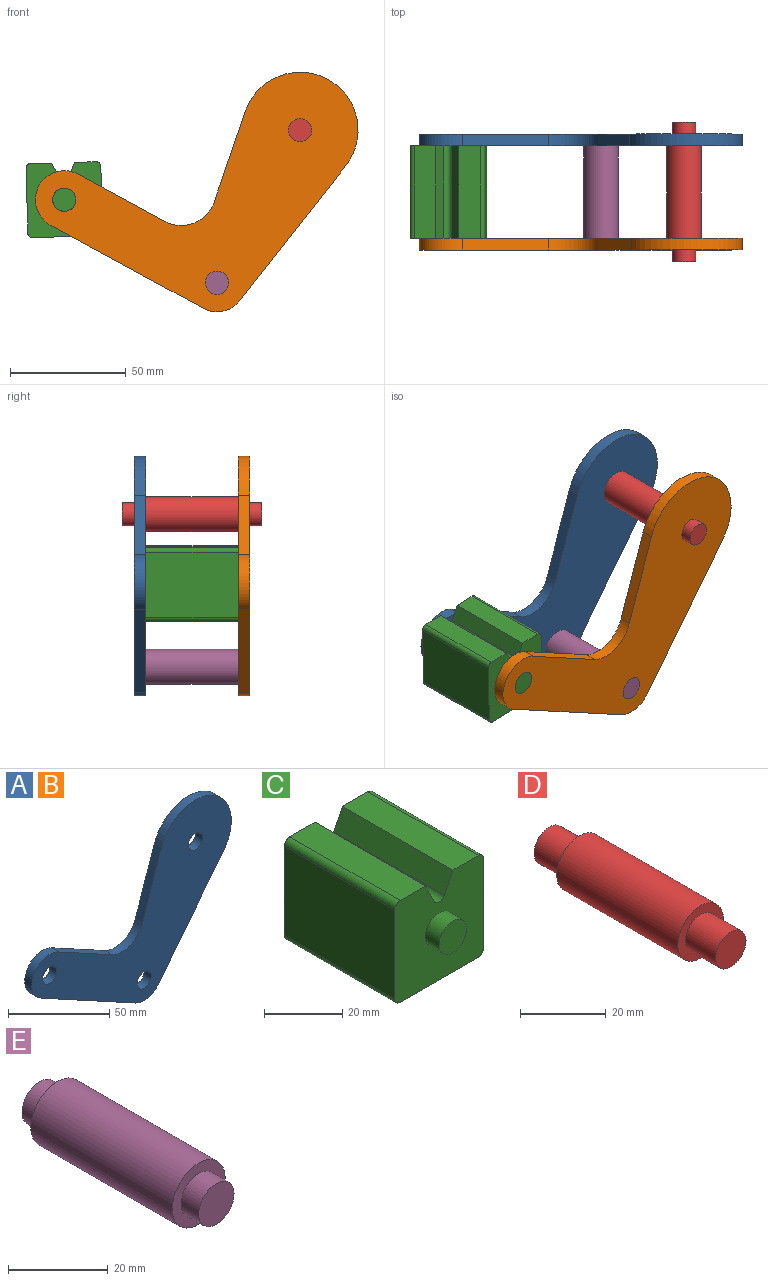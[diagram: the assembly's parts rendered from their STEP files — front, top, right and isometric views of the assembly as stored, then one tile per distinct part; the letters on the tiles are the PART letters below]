
ASSEMBLY  parts=5 mates=2
PART A: 13 faces, bbox 139.2x5x103.4 mm
  f0: cylinder r=25mm len=48.64mm, axis (0,-1,0), area 434.6mm2, adj f1,f9,f11,f12
  f1: plane 39.16x13.47mm, normal (-0.95,0,0.33), area 207.1mm2, adj f0,f2,f11,f12
  f2: cylinder r=15mm len=21.36mm, axis (0,-1,0), area 130.4mm2, adj f1,f3,f11,f12
  f3: plane 37.29x20.31mm, normal (0.48,0,0.88), area 212.3mm2, adj f2,f4,f11,f12
  f4: cylinder r=12.5mm len=23.48mm, axis (0,-1,0), area 196.3mm2, adj f3,f5,f11,f12
  f5: plane 65.87x35.87mm, normal (-0.48,0,-0.88), area 375mm2, adj f4,f6,f11,f12
  f6: cylinder r=12.5mm len=15.81mm, axis (0,-1,0), area 87.7mm2, adj f5,f9,f11,f12
  f7: cylinder r=5mm len=10mm, axis (0,-1,0), area 157.1mm2, adj f11,f12
  f8: cylinder r=5mm len=10mm, axis (0,-1,0), area 157.1mm2, adj f11,f12
  f9: plane 58.14x45.7mm, normal (0.79,0,-0.62), area 369.8mm2, adj f0,f6,f11,f12
  f10: cylinder r=5mm len=10mm, axis (0,-1,0), area 157.1mm2, adj f11,f12
  f11: plane 139.24x103.37mm, normal (0,1,0), area 5739.8mm2, adj f0,f1,f2,f3,f4,f5,f6,f7
  f12: plane 139.24x103.37mm, normal (0,-1,0), area 5739.8mm2, adj f0,f1,f2,f3,f4,f5,f6,f7
PART B: same geometry as A
PART C: 18 faces, bbox 32.3x50x31.9 mm
  f0: plane 40x9.14mm, normal (0,0,1), area 365.8mm2, adj f5,f7,f10,f14
  f1: plane 40x27.94mm, normal (-1,0,0), area 1117.4mm2, adj f7,f10,f14,f15
  f2: plane 40x28.29mm, normal (0,0,-1), area 1131.6mm2, adj f7,f10,f15,f16
  f3: plane 40x27.94mm, normal (1,0,0), area 1117.4mm2, adj f7,f10,f16,f17
  f4: plane 40x9.14mm, normal (0,0,1), area 365.8mm2, adj f6,f7,f10,f17
  f5: plane 40x6.42mm, normal (0.89,0,0.45), area 287.2mm2, adj f0,f7,f10,f13
  f6: plane 40x6.42mm, normal (-0.89,0,0.45), area 287.2mm2, adj f4,f7,f10,f13
  f7: plane 32.29x31.94mm, normal (0,-1,0), area 902.8mm2, adj f0,f1,f2,f3,f4,f5,f6,f8
  f8: cylinder r=5mm len=10mm, axis (0,-1,0), area 157.1mm2, adj f7,f9
  f9: plane 10x10mm, normal (0,-1,0), area 78.5mm2, adj f8
  f10: plane 32.29x31.94mm, normal (0,1,0), area 902.8mm2, adj f0,f1,f2,f3,f4,f5,f6,f11
  f11: cylinder r=5mm len=10mm, axis (0,1,0), area 157.1mm2, adj f10,f12
  f12: plane 10x10mm, normal (0,1,0), area 78.5mm2, adj f11
  f13: cylinder r=2mm len=40mm, axis (0,-1,0), area 177.1mm2, adj f5,f6,f7,f10
  f14: cylinder r=2mm len=40mm, axis (0,-1,0), area 125.7mm2, adj f0,f1,f7,f10
  f15: cylinder r=2mm len=40mm, axis (0,1,0), area 125.7mm2, adj f1,f2,f7,f10
  f16: cylinder r=2mm len=40mm, axis (0,-1,0), area 125.7mm2, adj f2,f3,f7,f10
  f17: cylinder r=2mm len=40mm, axis (0,1,0), area 125.7mm2, adj f3,f4,f7,f10
PART D: 7 faces, bbox 15x60x15 mm
  f0: cylinder r=7.5mm len=40mm, axis (0,-1,0), area 1885mm2, adj f2,f5
  f1: cylinder r=5mm len=10mm, axis (0,1,0), area 314.2mm2, adj f2,f3
  f2: plane 15x15mm, normal (0,-1,0), area 98.2mm2, adj f0,f1
  f3: plane 10x10mm, normal (0,-1,0), area 78.5mm2, adj f1
  f4: cylinder r=5mm len=10mm, axis (0,-1,0), area 314.2mm2, adj f5,f6
  f5: plane 15x15mm, normal (0,1,0), area 98.2mm2, adj f0,f4
  f6: plane 10x10mm, normal (0,1,0), area 78.5mm2, adj f4
PART E: 7 faces, bbox 15x50x15 mm
  f0: cylinder r=7.5mm len=40mm, axis (0,-1,0), area 1885mm2, adj f2,f5
  f1: cylinder r=5mm len=10mm, axis (0,-1,0), area 157.1mm2, adj f2,f3
  f2: plane 15x15mm, normal (0,-1,0), area 98.2mm2, adj f0,f1
  f3: plane 10x10mm, normal (0,-1,0), area 78.5mm2, adj f1
  f4: cylinder r=5mm len=10mm, axis (0,1,0), area 157.1mm2, adj f5,f6
  f5: plane 15x15mm, normal (0,1,0), area 98.2mm2, adj f0,f4
  f6: plane 10x10mm, normal (0,1,0), area 78.5mm2, adj f4
PLACE A t=(0,20,0)mm
PLACE B t=(0,-25,0)mm
PLACE C rot(axis=(0,-1,0),1.6deg) t=(-0.89,-25,2.86)mm
PLACE D t=(0,-25,0)mm fixed
PLACE E t=(0,-25,0)mm
MATE revolute C.f8 <-> B.f4  axis (0,-1,0) through (-101.73,-25,-30)mm
MATE fastened A.f6 <-> E.f0  axis (0,1,0) through (-35.87,25,-65.87)mm
